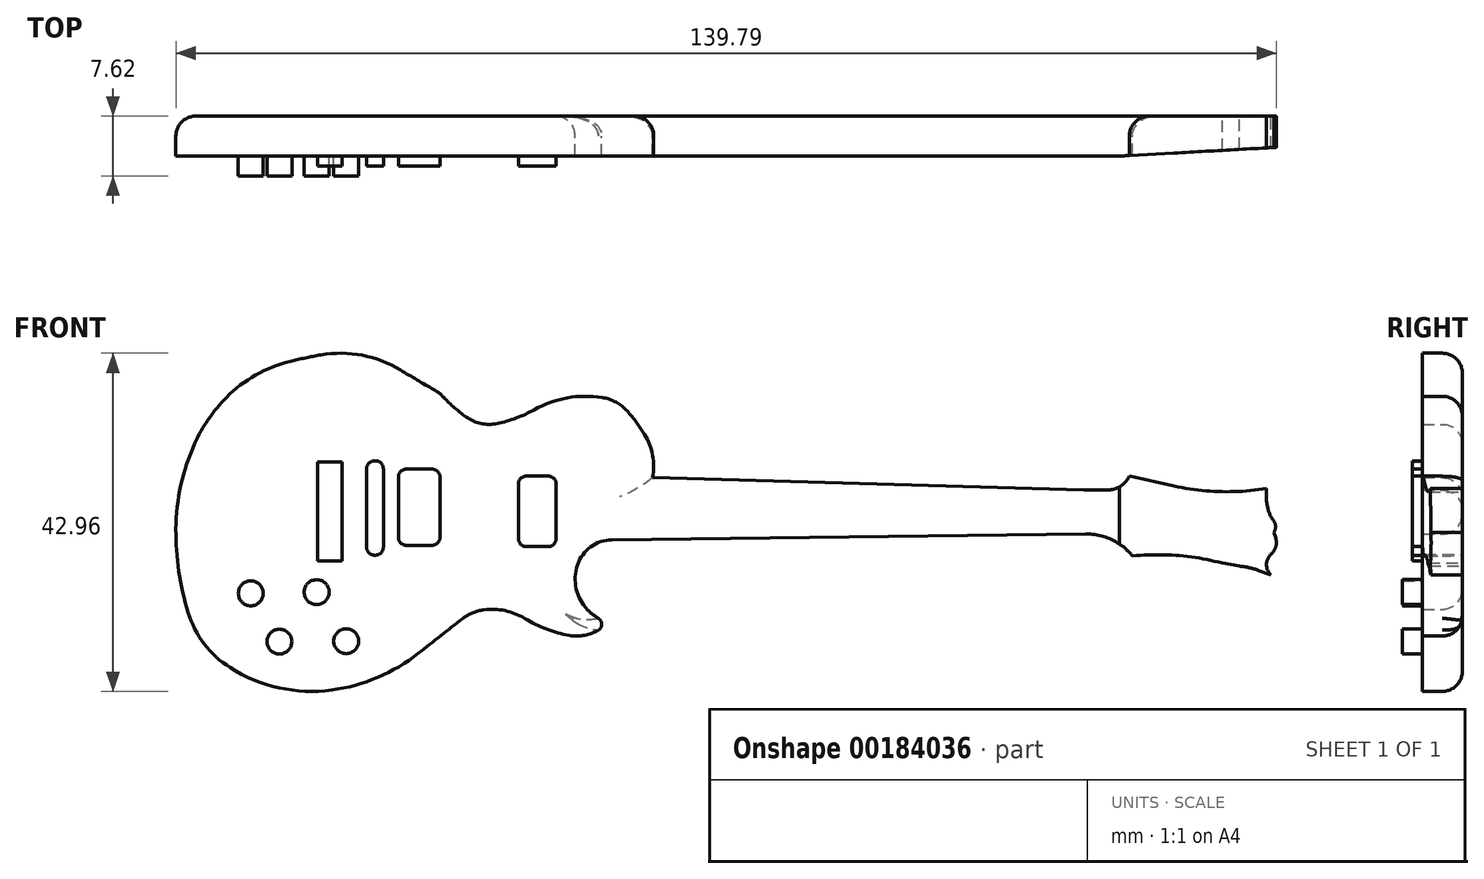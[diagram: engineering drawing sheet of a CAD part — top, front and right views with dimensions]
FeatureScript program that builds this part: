
annotation { "Feature Type Name" : "Feature", "Feature Type Description" : "" }
export const myFeature = defineFeature(function(context is Context, id is Id, definition is map)
    precondition{}
    {
        {
            var Q0;
            Q0=qCreatedBy(makeId("Front.planeOp"),FACE);
            var sketch = newSketch(context, id + "F0", { "sketchPlane" : qUnion([Q0])});
            skLineSegment(sketch, "E0", {"start": v(44.6, 23.47) * mm, "end": v(-15.58, 22.73) * mm});
            skArc(sketch, "E1", {"start": v(-15.58, 22.73) * mm, "mid": v(-18.3, 21.83) * mm, "end": v(-19.99, 19.52) * mm});
            skArc(sketch, "E2", {"start": v(-19.99, 19.52) * mm, "mid": v(-20.14, 16.5) * mm, "end": v(-18.7, 13.83) * mm});
            skArc(sketch, "E3", {"start": v(-18.7, 13.83) * mm, "mid": v(-18.05, 13.24) * mm, "end": v(-17.33, 12.73) * mm});
            skArc(sketch, "E4", {"start": v(-17.33, 12.73) * mm, "mid": v(-16.91, 12) * mm, "end": v(-17.33, 11.26) * mm});
            skArc(sketch, "E5", {"start": v(-17.33, 11.26) * mm, "mid": v(-19.1, 10.59) * mm, "end": v(-20.99, 10.58) * mm});
            skArc(sketch, "E6", {"start": v(-20.99, 10.58) * mm, "mid": v(-23.94, 11.4) * mm, "end": v(-26.69, 12.73) * mm});
            skArc(sketch, "E7", {"start": v(-26.69, 12.73) * mm, "mid": v(-29.2, 13.72) * mm, "end": v(-31.89, 13.83) * mm});
            skArc(sketch, "E8", {"start": v(-31.89, 13.83) * mm, "mid": v(-33.29, 13.46) * mm, "end": v(-34.54, 12.73) * mm});
            skArc(sketch, "E9", {"start": v(-34.54, 12.73) * mm, "mid": v(-37.37, 10.54) * mm, "end": v(-40.17, 8.33) * mm});
            skArc(sketch, "E10", {"start": v(-40.17, 8.33) * mm, "mid": v(-45.36, 5.24) * mm, "end": v(-51.18, 3.65) * mm});
            skArc(sketch, "E11", {"start": v(-51.18, 3.65) * mm, "mid": v(-57.9, 3.92) * mm, "end": v(-64.12, 6.5) * mm});
            skArc(sketch, "E12", {"start": v(-64.12, 6.5) * mm, "mid": v(-67.4, 9.5) * mm, "end": v(-69.44, 13.46) * mm});
            skArc(sketch, "E13", {"start": v(-69.44, 13.46) * mm, "mid": v(-70.63, 18.73) * mm, "end": v(-71, 24.1) * mm});
            skArc(sketch, "E14", {"start": v(-71, 24.1) * mm, "mid": v(-70.37, 29.65) * mm, "end": v(-68.62, 34.93) * mm});
            skArc(sketch, "E15", {"start": v(-68.62, 34.93) * mm, "mid": v(-66.86, 38.05) * mm, "end": v(-64.58, 40.8) * mm});
            skArc(sketch, "E16", {"start": v(-64.58, 40.8) * mm, "mid": v(-60.86, 43.66) * mm, "end": v(-56.5, 45.4) * mm});
            skArc(sketch, "E17", {"start": v(-56.5, 45.4) * mm, "mid": v(-54.54, 45.84) * mm, "end": v(-52.56, 46.22) * mm});
            skArc(sketch, "E18", {"start": v(-52.56, 46.22) * mm, "mid": v(-47.34, 46.17) * mm, "end": v(-42.47, 44.3) * mm});
            skArc(sketch, "E19", {"start": v(-42.47, 44.3) * mm, "mid": v(-40.37, 43.04) * mm, "end": v(-38.25, 41.82) * mm});
            skArc(sketch, "E20", {"start": v(-38.25, 41.82) * mm, "mid": v(-37.57, 41.36) * mm, "end": v(-36.96, 40.8) * mm});
            skArc(sketch, "E21", {"start": v(-36.96, 40.8) * mm, "mid": v(-35.6, 39.5) * mm, "end": v(-34.12, 38.33) * mm});
            skArc(sketch, "E22", {"start": v(-34.12, 38.33) * mm, "mid": v(-32.23, 37.5) * mm, "end": v(-30.17, 37.5) * mm});
            skArc(sketch, "E23", {"start": v(-30.17, 37.5) * mm, "mid": v(-27.76, 38.2) * mm, "end": v(-25.5, 39.25) * mm});
            skArc(sketch, "E24", {"start": v(-25.5, 39.25) * mm, "mid": v(-21.31, 40.75) * mm, "end": v(-16.87, 40.8) * mm});
            skArc(sketch, "E25", {"start": v(-16.87, 40.8) * mm, "mid": v(-15.11, 40.21) * mm, "end": v(-13.66, 39.06) * mm});
            skArc(sketch, "E26", {"start": v(-13.66, 39.06) * mm, "mid": v(-12.5, 37.64) * mm, "end": v(-11.45, 36.13) * mm});
            skArc(sketch, "E27", {"start": v(-11.45, 36.13) * mm, "mid": v(-10.43, 33.47) * mm, "end": v(-10.45, 30.62) * mm});
            skLineSegment(sketch, "E28", {"start": v(-10.45, 30.62) * mm, "end": v(44.33, 29.06) * mm});
            skArc(sketch, "E29", {"start": v(44.33, 29.06) * mm, "mid": v(45.89, 29.04) * mm, "end": v(47.45, 29.06) * mm});
            skArc(sketch, "E30", {"start": v(47.45, 29.06) * mm, "mid": v(49.03, 29.56) * mm, "end": v(50.1, 30.8) * mm});
            skLineSegment(sketch, "E31", {"start": v(50.1, 30.8) * mm, "end": v(55.8, 29.56) * mm});
            skPoint(sketch, "E31.endSnap0", {"position": v(49.03, 29.56) * mm});
            skArc(sketch, "E32", {"start": v(55.8, 29.56) * mm, "mid": v(61.65, 28.84) * mm, "end": v(67.54, 29.25) * mm});
            skLineSegment(sketch, "E33", {"start": v(67.54, 29.25) * mm, "end": v(67.54, 28) * mm});
            skArc(sketch, "E34", {"start": v(67.54, 28) * mm, "mid": v(67.78, 26.48) * mm, "end": v(68.47, 25.1) * mm});
            skArc(sketch, "E35", {"start": v(68.47, 25.1) * mm, "mid": v(68.7, 24.38) * mm, "end": v(68.47, 23.66) * mm});
            skLineSegment(sketch, "E36", {"start": v(68.47, 23.66) * mm, "end": v(68.7, 22.95) * mm});
            skPoint(sketch, "E36.endSnap0", {"position": v(68.7, 24.38) * mm});
            skArc(sketch, "E37", {"start": v(68.7, 22.95) * mm, "mid": v(68.72, 21.86) * mm, "end": v(68.15, 20.94) * mm});
            skArc(sketch, "E38", {"start": v(68.15, 20.94) * mm, "mid": v(67.53, 19.62) * mm, "end": v(68.08, 18.28) * mm});
            skLineSegment(sketch, "E39", {"start": v(68.08, 18.28) * mm, "end": v(66.46, 18.86) * mm});
            skArc(sketch, "E40", {"start": v(66.46, 18.86) * mm, "mid": v(65.3, 19.2) * mm, "end": v(64.12, 19.38) * mm});
            skArc(sketch, "E41", {"start": v(61.92, 19.77) * mm, "mid": v(56.25, 20.73) * mm, "end": v(50.5, 20.68) * mm});
            skLineSegment(sketch, "E42", {"start": v(64.12, 19.38) * mm, "end": v(61.92, 19.77) * mm});
            skArc(sketch, "E43", {"start": v(44.6, 23.47) * mm, "mid": v(47.87, 22.75) * mm, "end": v(50.5, 20.68) * mm});
            skPoint(sketch, "E44", {"position": v(-15.58, 22.73) * mm});
            skSolve(sketch);
        }
        {
            var Q0;
            Q0 = qSketchRegion(id + "F0", true);
            extrude(context, id + "F1", {"entities" : qUnion([Q0]), "depth" : 5.08 * mm});
        }
        {
            var Q0;
            Q0=makeQuery(id+"F1.opExtrude","CAP_FACE",FACE,{"disambiguationData":[OSD([sQuery(id+"F0.wireOp",EDGE,"E0"),sQuery(id+"F0.wireOp",EDGE,"E1"),sQuery(id+"F0.wireOp",EDGE,"E2"),sQuery(id+"F0.wireOp",EDGE,"E3"),sQuery(id+"F0.wireOp",EDGE,"E4"),sQuery(id+"F0.wireOp",EDGE,"E5"),sQuery(id+"F0.wireOp",EDGE,"E6"),sQuery(id+"F0.wireOp",EDGE,"E7"),sQuery(id+"F0.wireOp",EDGE,"E8"),sQuery(id+"F0.wireOp",EDGE,"E9"),sQuery(id+"F0.wireOp",EDGE,"E10"),sQuery(id+"F0.wireOp",EDGE,"E11"),sQuery(id+"F0.wireOp",EDGE,"E12"),sQuery(id+"F0.wireOp",EDGE,"E13"),sQuery(id+"F0.wireOp",EDGE,"E14"),sQuery(id+"F0.wireOp",EDGE,"E15"),sQuery(id+"F0.wireOp",EDGE,"E16"),sQuery(id+"F0.wireOp",EDGE,"E17"),sQuery(id+"F0.wireOp",EDGE,"E18"),sQuery(id+"F0.wireOp",EDGE,"E19"),sQuery(id+"F0.wireOp",EDGE,"E20"),sQuery(id+"F0.wireOp",EDGE,"E21"),sQuery(id+"F0.wireOp",EDGE,"E22"),sQuery(id+"F0.wireOp",EDGE,"E23"),sQuery(id+"F0.wireOp",EDGE,"E24"),sQuery(id+"F0.wireOp",EDGE,"E25"),sQuery(id+"F0.wireOp",EDGE,"E26"),sQuery(id+"F0.wireOp",EDGE,"E27"),sQuery(id+"F0.wireOp",EDGE,"E28"),sQuery(id+"F0.wireOp",EDGE,"E29"),sQuery(id+"F0.wireOp",EDGE,"E30"),sQuery(id+"F0.wireOp",EDGE,"E31"),sQuery(id+"F0.wireOp",EDGE,"E32"),sQuery(id+"F0.wireOp",EDGE,"E33"),sQuery(id+"F0.wireOp",EDGE,"E34"),sQuery(id+"F0.wireOp",EDGE,"E35"),sQuery(id+"F0.wireOp",EDGE,"E36"),sQuery(id+"F0.wireOp",EDGE,"E37"),sQuery(id+"F0.wireOp",EDGE,"E38"),sQuery(id+"F0.wireOp",EDGE,"E39"),sQuery(id+"F0.wireOp",EDGE,"E40"),sQuery(id+"F0.wireOp",EDGE,"E41"),sQuery(id+"F0.wireOp",EDGE,"E42"),sQuery(id+"F0.wireOp",EDGE,"E43")])],"isStart":false});
            var sketch = newSketch(context, id + "F2", { "sketchPlane" : qUnion([Q0])});
            skLineSegment(sketch, "E45.bottom", {"start": v(-22.7, 30.81) * mm, "end": v(-27.5, 30.81) * mm});
            skLineSegment(sketch, "E45.top", {"start": v(-22.7, 21.87) * mm, "end": v(-27.5, 21.87) * mm});
            skLineSegment(sketch, "E45.left", {"start": v(-22.7, 30.81) * mm, "end": v(-22.7, 21.87) * mm});
            skLineSegment(sketch, "E45.right", {"start": v(-27.5, 30.81) * mm, "end": v(-27.5, 21.87) * mm});
            skLineSegment(sketch, "E46.bottom", {"start": v(-37.44, 31.7) * mm, "end": v(-42.74, 31.7) * mm});
            skLineSegment(sketch, "E46.top", {"start": v(-37.44, 22.03) * mm, "end": v(-42.74, 22.03) * mm});
            skLineSegment(sketch, "E46.left", {"start": v(-37.44, 31.7) * mm, "end": v(-37.44, 22.03) * mm});
            skLineSegment(sketch, "E46.right", {"start": v(-42.74, 31.7) * mm, "end": v(-42.74, 22.03) * mm});
            skLineSegment(sketch, "E47.bottom", {"start": v(-53, 32.63) * mm, "end": v(-49.86, 32.63) * mm});
            skLineSegment(sketch, "E47.top", {"start": v(-53, 20.04) * mm, "end": v(-49.86, 20.04) * mm});
            skLineSegment(sketch, "E47.left", {"start": v(-53, 32.63) * mm, "end": v(-53, 20.04) * mm});
            skLineSegment(sketch, "E47.right", {"start": v(-49.86, 32.63) * mm, "end": v(-49.86, 20.04) * mm});
            skLineSegment(sketch, "E48.bottom", {"start": v(-46.78, 20.77) * mm, "end": v(-44.65, 20.77) * mm});
            skLineSegment(sketch, "E48.top", {"start": v(-46.78, 32.76) * mm, "end": v(-44.65, 32.76) * mm});
            skLineSegment(sketch, "E48.left", {"start": v(-46.78, 20.77) * mm, "end": v(-46.78, 32.76) * mm});
            skLineSegment(sketch, "E48.right", {"start": v(-44.65, 20.77) * mm, "end": v(-44.65, 32.76) * mm});
            skSolve(sketch);
        }
        {
            var Q0;
            Q0 = qSketchRegion(id + "F2", true);
            extrude(context, id + "F3", {"entities" : qUnion([Q0]), "operationType" : NewBodyOperationType.ADD, "depth" : 1.27 * mm});
        }
        {
            var Q0;
            Q0=makeQuery(id+"F2.imprint","IMPRINT",FACE,{"disambiguationData":[TD([[makeQuery(id+"F2.imprint","IMPRINT",EDGE,{"derivedFrom":sQuery(id+"F2.wireOp",EDGE,"E45.bottom")}),-1.0]])]});
            var sketch = newSketch(context, id + "F4", { "sketchPlane" : qUnion([Q0])});
            skCircle(sketch, "E49", {"center": v(-61.49, 15.93) * mm, "radius": 1.59 * mm});
            skPoint(sketch, "E49.first.point", {"position": v(-60.6, 17.25) * mm});
            skPoint(sketch, "E49.second.point", {"position": v(-63.06, 15.77) * mm});
            skPoint(sketch, "E49.third.point", {"position": v(-60.92, 14.45) * mm});
            skCircle(sketch, "E50", {"center": v(-53.12, 16.07) * mm, "radius": 1.59 * mm});
            skPoint(sketch, "E50.first.point", {"position": v(-54.4, 17.02) * mm});
            skPoint(sketch, "E50.second.point", {"position": v(-51.54, 16.26) * mm});
            skPoint(sketch, "E50.third.point", {"position": v(-51.7, 15.34) * mm});
            skCircle(sketch, "E51", {"center": v(-49.36, 9.85) * mm, "radius": 1.59 * mm});
            skPoint(sketch, "E51.first.point", {"position": v(-50.38, 11.07) * mm});
            skPoint(sketch, "E51.second.point", {"position": v(-48.35, 8.62) * mm});
            skPoint(sketch, "E51.third.point", {"position": v(-50.52, 8.76) * mm});
            skCircle(sketch, "E52", {"center": v(-57.85, 9.79) * mm, "radius": 1.59 * mm});
            skPoint(sketch, "E52.first.point", {"position": v(-57.26, 8.31) * mm});
            skPoint(sketch, "E52.second.point", {"position": v(-58.38, 11.29) * mm});
            skPoint(sketch, "E52.third.point", {"position": v(-59.42, 9.5) * mm});
            skSolve(sketch);
        }
        {
            var Q0;
            Q0 = qSketchRegion(id + "F4", true);
            extrude(context, id + "F5", {"entities" : qUnion([Q0]), "operationType" : NewBodyOperationType.ADD, "depth" : 2.54 * mm});
        }
        {
            var Q0;
            Q0=makeQuery(id+"F1.opExtrude","CAP_EDGE",EDGE,{"disambiguationData":[OSD([sQuery(id+"F0.wireOp",EDGE,"E0")])],"isStart":true});
            var Q1;
            Q1=makeQuery(id+"F1.opExtrude","CAP_EDGE",EDGE,{"disambiguationData":[OSD([sQuery(id+"F0.wireOp",EDGE,"E28")])],"isStart":true});
            fillet(context, id + "F6", {"entities" : qUnion([Q0, Q1]), "radius" : 2.54 * mm, "tangentPropagation" : true, "allowEdgeOverflow" : false});
        }
        {
            var Q0;
            Q0=qCreatedBy(makeId("Top.planeOp"),FACE);
            var sketch = newSketch(context, id + "F7", { "sketchPlane" : qUnion([Q0])});
            skLineSegment(sketch, "E53", {"start": v(39.16, -5.62) * mm, "end": v(72.7, -3.75) * mm});
            skLineSegment(sketch, "E54", {"start": v(72.7, -3.75) * mm, "end": v(71.44, -9.77) * mm});
            skLineSegment(sketch, "E55", {"start": v(71.44, -9.77) * mm, "end": v(39.16, -5.62) * mm});
            skSolve(sketch);
        }
        {
            var Q0;
            Q0=makeQuery(id+"F7.imprint","IMPRINT",FACE,{"disambiguationData":[TD([[makeQuery(id+"F7.imprint","IMPRINT",EDGE,{"derivedFrom":sQuery(id+"F7.wireOp",EDGE,"E53")}),-1.0]])]});
            extrude(context, id + "F8", {"entities" : qUnion([Q0]), "operationType" : NewBodyOperationType.REMOVE, "depth" : 50.8 * mm});
        }
        {
            var Q0;
            Q0=makeQuery(id+"F3.opExtrude","SWEPT_EDGE",EDGE,{"disambiguationData":[OSD([sQuery(id+"F2.wireOp",EDGE,"E48.top"),sQuery(id+"F2.wireOp",EDGE,"E48.right")])]});
            var Q1;
            Q1=makeQuery(id+"F3.opExtrude","SWEPT_EDGE",EDGE,{"disambiguationData":[OSD([sQuery(id+"F2.wireOp",EDGE,"E48.top"),sQuery(id+"F2.wireOp",EDGE,"E48.left")])]});
            var Q2;
            Q2=makeQuery(id+"F3.opExtrude","SWEPT_EDGE",EDGE,{"disambiguationData":[OSD([sQuery(id+"F2.wireOp",EDGE,"E48.bottom"),sQuery(id+"F2.wireOp",EDGE,"E48.left")])]});
            var Q3;
            Q3=makeQuery(id+"F3.opExtrude","SWEPT_EDGE",EDGE,{"disambiguationData":[OSD([sQuery(id+"F2.wireOp",EDGE,"E48.bottom"),sQuery(id+"F2.wireOp",EDGE,"E48.right")])]});
            fillet(context, id + "F9", {"entities" : qUnion([Q0, Q1, Q2, Q3]), "radius" : 1.02 * mm, "tangentPropagation" : true, "allowEdgeOverflow" : false});
        }
        {
            var Q0;
            Q0=makeQuery(id+"F3.opExtrude","SWEPT_EDGE",EDGE,{"disambiguationData":[OSD([sQuery(id+"F2.wireOp",EDGE,"E46.bottom"),sQuery(id+"F2.wireOp",EDGE,"E46.left")])]});
            var Q1;
            Q1=makeQuery(id+"F3.opExtrude","SWEPT_EDGE",EDGE,{"disambiguationData":[OSD([sQuery(id+"F2.wireOp",EDGE,"E46.bottom"),sQuery(id+"F2.wireOp",EDGE,"E46.right")])]});
            var Q2;
            Q2=makeQuery(id+"F3.opExtrude","SWEPT_EDGE",EDGE,{"disambiguationData":[OSD([sQuery(id+"F2.wireOp",EDGE,"E46.top"),sQuery(id+"F2.wireOp",EDGE,"E46.right")])]});
            var Q3;
            Q3=makeQuery(id+"F3.opExtrude","SWEPT_EDGE",EDGE,{"disambiguationData":[OSD([sQuery(id+"F2.wireOp",EDGE,"E46.top"),sQuery(id+"F2.wireOp",EDGE,"E46.left")])]});
            var Q4;
            Q4=makeQuery(id+"F3.opExtrude","SWEPT_EDGE",EDGE,{"disambiguationData":[OSD([sQuery(id+"F2.wireOp",EDGE,"E45.top"),sQuery(id+"F2.wireOp",EDGE,"E45.left")])]});
            var Q5;
            Q5=makeQuery(id+"F3.opExtrude","SWEPT_EDGE",EDGE,{"disambiguationData":[OSD([sQuery(id+"F2.wireOp",EDGE,"E45.top"),sQuery(id+"F2.wireOp",EDGE,"E45.right")])]});
            var Q6;
            Q6=makeQuery(id+"F3.opExtrude","SWEPT_EDGE",EDGE,{"disambiguationData":[OSD([sQuery(id+"F2.wireOp",EDGE,"E45.bottom"),sQuery(id+"F2.wireOp",EDGE,"E45.right")])]});
            var Q7;
            Q7=makeQuery(id+"F3.opExtrude","SWEPT_EDGE",EDGE,{"disambiguationData":[OSD([sQuery(id+"F2.wireOp",EDGE,"E45.bottom"),sQuery(id+"F2.wireOp",EDGE,"E45.left")])]});
            fillet(context, id + "F10", {"entities" : qUnion([Q0, Q1, Q2, Q3, Q4, Q5, Q6, Q7]), "radius" : 1.02 * mm, "tangentPropagation" : true, "allowEdgeOverflow" : false});
        }
    });
